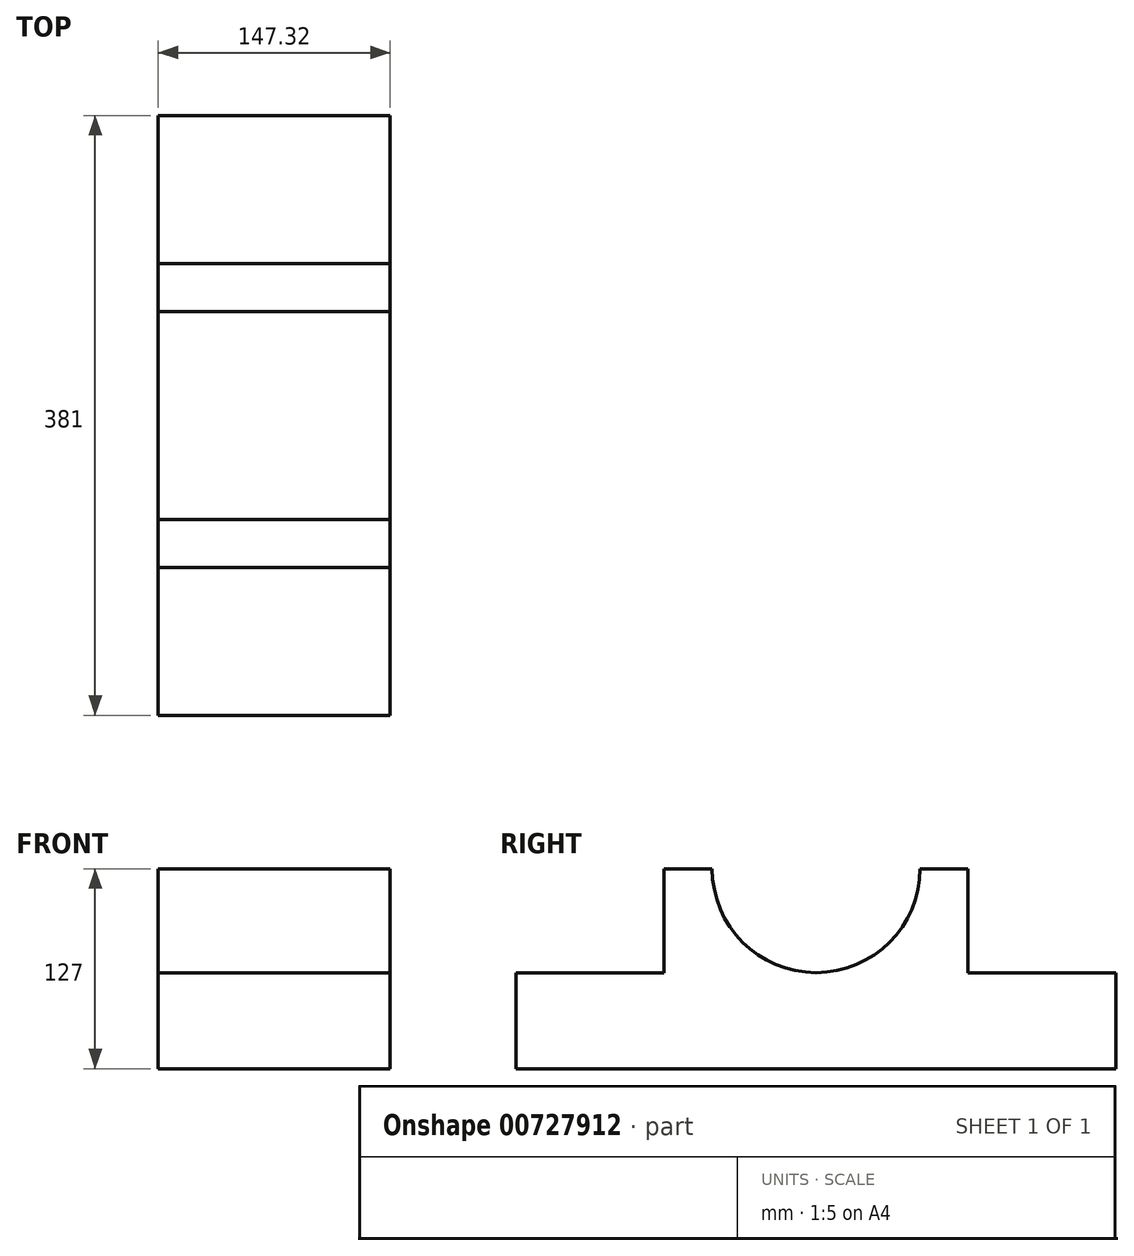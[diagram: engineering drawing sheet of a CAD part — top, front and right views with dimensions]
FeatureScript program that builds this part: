
annotation { "Feature Type Name" : "Feature", "Feature Type Description" : "" }
export const myFeature = defineFeature(function(context is Context, id is Id, definition is map)
    precondition{}
    {
        {
            var Q0;
            Q0=qCreatedBy(makeId("Right.planeOp"),FACE);
            var sketch = newSketch(context, id + "F0", { "sketchPlane" : qUnion([Q0])});
            skLineSegment(sketch, "E0", {"start": v(-227.21, -133.6) * mm, "end": v(153.79, -133.6) * mm});
            skLineSegment(sketch, "E1", {"start": v(-227.21, -133.6) * mm, "end": v(-227.21, -72.64) * mm});
            skLineSegment(sketch, "E2", {"start": v(-227.21, -72.64) * mm, "end": v(-133.23, -72.64) * mm});
            skLineSegment(sketch, "E3", {"start": v(-133.23, -72.64) * mm, "end": v(-133.23, -6.6) * mm});
            skLineSegment(sketch, "E4", {"start": v(-133.23, -6.6) * mm, "end": v(-97.46, -6.6) * mm});
            skLineSegment(sketch, "E5", {"start": v(-3.42, -6.6) * mm, "end": v(59.8, -6.6) * mm});
            skLineSegment(sketch, "E6", {"start": v(59.8, -6.6) * mm, "end": v(59.8, -72.64) * mm});
            skLineSegment(sketch, "E7", {"start": v(59.8, -72.64) * mm, "end": v(153.79, -72.64) * mm});
            skLineSegment(sketch, "E8", {"start": v(153.79, -72.64) * mm, "end": v(153.79, -133.6) * mm});
            skLineSegment(sketch, "E9", {"start": v(-97.46, -6.6) * mm, "end": v(-3.42, -6.6) * mm});
            skSolve(sketch);
        }
        {
            var Q0;
            Q0=makeQuery(id+"F0.imprint","IMPRINT",FACE,{"disambiguationData":[TD([[makeQuery(id+"F0.imprint","IMPRINT",EDGE,{"derivedFrom":sQuery(id+"F0.wireOp",EDGE,"E0")}),1.0]])]});
            var sketch = newSketch(context, id + "F1", { "sketchPlane" : qUnion([Q0])});
            skCircle(sketch, "E10", {"center": v(-36.71, -6.58) * mm, "radius": 66.04 * mm});
            skPoint(sketch, "E11", {"position": v(-102.75, -6.58) * mm});
            skPoint(sketch, "E12", {"position": v(29.33, -6.58) * mm});
            skSolve(sketch);
        }
        {
            var Q0;
            Q0=makeQuery(id+"F0.imprint","IMPRINT",FACE,{"disambiguationData":[TD([[makeQuery(id+"F0.imprint","IMPRINT",EDGE,{"derivedFrom":sQuery(id+"F0.wireOp",EDGE,"E0")}),1.0]])]});
            extrude(context, id + "F2", {"entities" : qUnion([Q0]), "depth" : 147.32 * mm, "offsetDistance" : 25.4 * mm});
        }
        {
            var Q0;
            {var subQ5=makeQuery(id+"F0.imprint","IMPRINT",EDGE,{"derivedFrom":sQuery(id+"F0.wireOp",EDGE,"E9")});Q0=makeQuery(id+"F1.imprint","IMPRINT",FACE,{"disambiguationData":[TD([[makeQuery(id+"F1.imprint","IMPRINT",EDGE,{"derivedFrom":subQ5}),1.0]])]});}
            extrude(context, id + "F3", {"entities" : qUnion([Q0]), "operationType" : NewBodyOperationType.REMOVE, "endBound" : BoundingType.THROUGH_ALL, "oppositeDirection" : true, "depth" : 25.4 * mm, "offsetDistance" : 25.4 * mm});
        }
        {
            var Q0;
            Q0 = qSketchRegion(id + "F1", true);
            var Q1;
            Q1=makeQuery(id+"F2.opExtrude","CAP_FACE",FACE,{"disambiguationData":[OSD([sQuery(id+"F0.wireOp",EDGE,"E0"),sQuery(id+"F0.wireOp",EDGE,"E1"),sQuery(id+"F0.wireOp",EDGE,"E2"),sQuery(id+"F0.wireOp",EDGE,"E3"),sQuery(id+"F0.wireOp",EDGE,"E4"),sQuery(id+"F0.wireOp",EDGE,"E5"),sQuery(id+"F0.wireOp",EDGE,"E6"),sQuery(id+"F0.wireOp",EDGE,"E7"),sQuery(id+"F0.wireOp",EDGE,"E8"),sQuery(id+"F0.wireOp",EDGE,"E9")])],"isStart":false});
            extrude(context, id + "F4", {"entities" : qUnion([Q0, Q1]), "operationType" : NewBodyOperationType.REMOVE, "endBound" : BoundingType.THROUGH_ALL, "depth" : 25.4 * mm, "offsetDistance" : 25.4 * mm});
        }
    });
